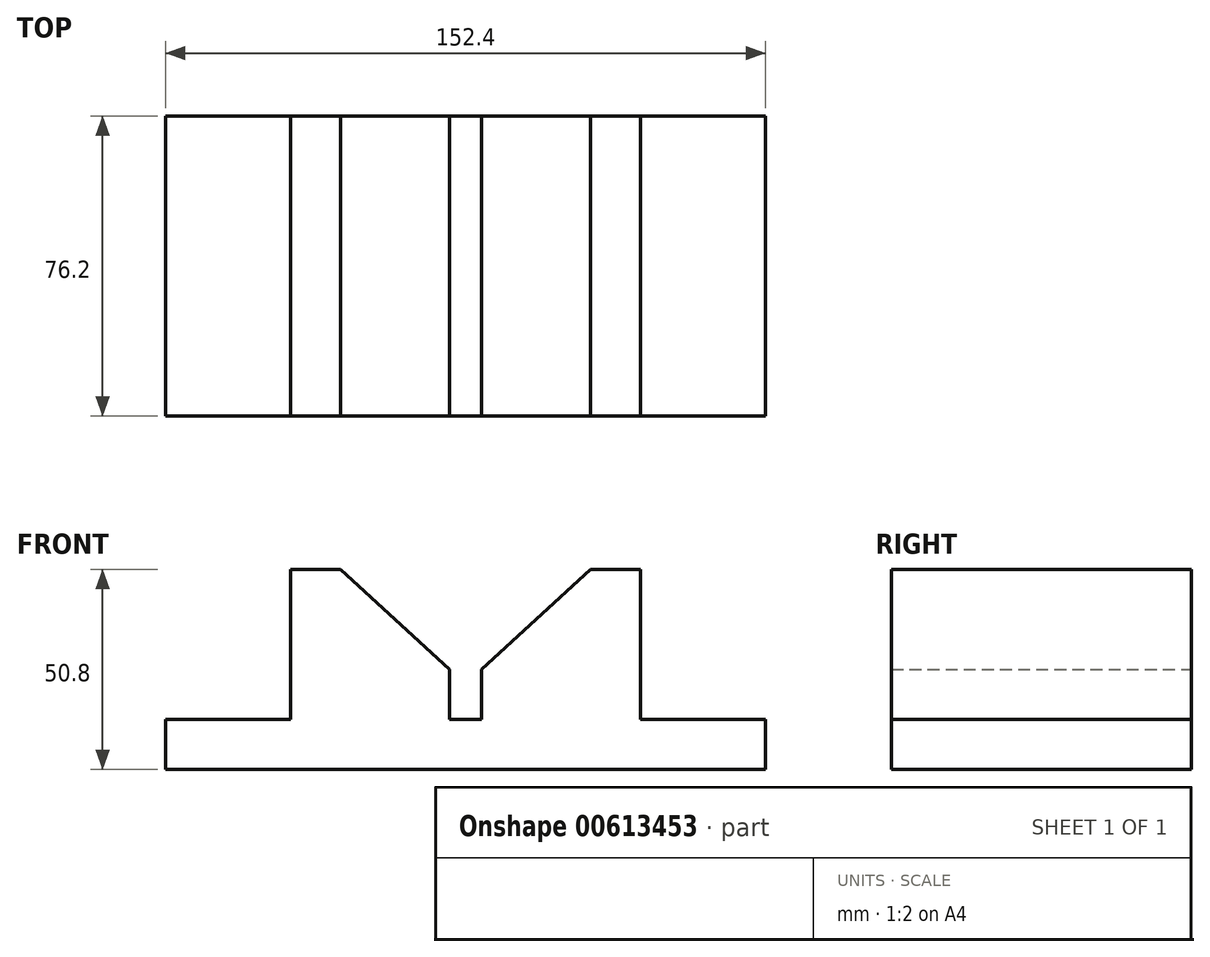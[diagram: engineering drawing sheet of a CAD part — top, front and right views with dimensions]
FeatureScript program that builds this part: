
annotation { "Feature Type Name" : "Feature", "Feature Type Description" : "" }
export const myFeature = defineFeature(function(context is Context, id is Id, definition is map)
    precondition{}
    {
        {
            var Q0;
            Q0=qCreatedBy(makeId("Front.planeOp"),FACE);
            var sketch = newSketch(context, id + "F0", { "sketchPlane" : qUnion([Q0])});
            skLineSegment(sketch, "E0", {"start": v(0, 0) * mm, "end": v(0, 12.7) * mm});
            skLineSegment(sketch, "E1", {"start": v(0, 12.7) * mm, "end": v(31.75, 12.7) * mm});
            skLineSegment(sketch, "E2", {"start": v(31.75, 12.7) * mm, "end": v(31.75, 50.8) * mm});
            skLineSegment(sketch, "E3", {"start": v(31.75, 50.8) * mm, "end": v(44.45, 50.8) * mm});
            skLineSegment(sketch, "E4", {"start": v(44.45, 50.8) * mm, "end": v(72.11, 25.4) * mm});
            skLineSegment(sketch, "E5", {"start": v(72.11, 25.4) * mm, "end": v(72.11, 12.7) * mm});
            skLineSegment(sketch, "E6", {"start": v(72.11, 12.7) * mm, "end": v(80.27, 12.7) * mm});
            skLineSegment(sketch, "E7", {"start": v(80.27, 12.7) * mm, "end": v(80.27, 25.4) * mm});
            skLineSegment(sketch, "E8", {"start": v(80.27, 25.4) * mm, "end": v(107.95, 50.8) * mm});
            skLineSegment(sketch, "E9", {"start": v(107.95, 50.8) * mm, "end": v(120.65, 50.8) * mm});
            skLineSegment(sketch, "E10", {"start": v(120.65, 50.8) * mm, "end": v(120.65, 12.7) * mm});
            skLineSegment(sketch, "E11", {"start": v(120.65, 12.7) * mm, "end": v(152.4, 12.7) * mm});
            skLineSegment(sketch, "E12", {"start": v(152.4, 12.7) * mm, "end": v(152.4, 0) * mm});
            skLineSegment(sketch, "E13", {"start": v(152.4, 0) * mm, "end": v(0, 0) * mm});
            skSolve(sketch);
        }
        {
            var Q0;
            Q0=makeQuery(id+"F0.imprint","IMPRINT",FACE,{"disambiguationData":[TD([[makeQuery(id+"F0.imprint","IMPRINT",EDGE,{"derivedFrom":sQuery(id+"F0.wireOp",EDGE,"E0")}),-1.0]])]});
            extrude(context, id + "F1", {"entities" : qUnion([Q0]), "depth" : 76.2 * mm, "offsetDistance" : 25.4 * mm});
        }
    });
